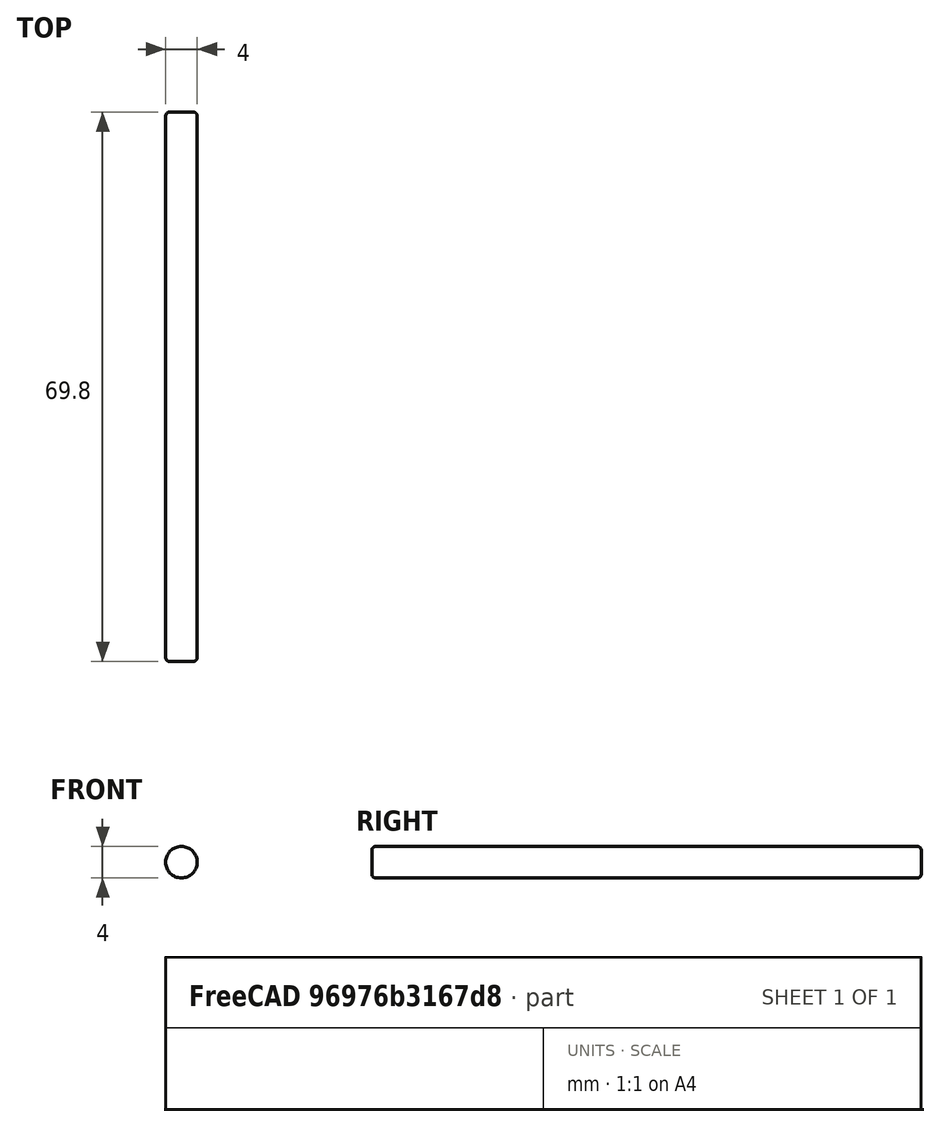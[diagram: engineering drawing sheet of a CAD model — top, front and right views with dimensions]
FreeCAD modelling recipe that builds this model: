
FCSTD DOCUMENT  (FreeCAD 0.19R24267 +99 (Git))
Label: Achse
License: All rights reserved
LicenseURL: http://en.wikipedia.org/wiki/All_rights_reserved
objects: TechDraw::DrawViewDimension×4, TechDraw::DrawProjGroupItem×3, Sketcher::SketchObject×1, PartDesign::Pad×1, PartDesign::Fillet×1, PartDesign::Body×1, TechDraw::DrawSVGTemplate×1, TechDraw::DrawProjGroup×1, TechDraw::DrawPage×1
note: 6 computed .brp shape members not serialized (recipe doc carries the construction recipe); baked Part::Feature solids carry a one-line shape summary decoded from their .brp

FEATURE [Sketcher::SketchObject] Sketch
  FullyConstrained = true
  MapMode = 5
  Placement = pos=(0,0,0) rot=(1,0,0;1.5708rad)
  Support = -> [XZ_Plane]
  sketch-geometry (1):
    g0: Circle CenterX=0 CenterY=0 CenterZ=0 NormalX=0 NormalY=0 NormalZ=1 AngleXU=0 Radius=2
  constraints (2):
    c: Coincident(g0,g-1)
    c: Diameter(g0) = 4
FEATURE [PartDesign::Pad] Pad
  Direction = (1,1,1)
  Length = 69.8
  Length2 = 100
  Placement = pos=(0,0,0) rot=(1,0,0;1.5708rad)
  Profile = -> Sketch
  Type = 0
FEATURE [PartDesign::Fillet] Fillet
  Base = -> Pad [Edge3,Edge2]
  BaseFeature = -> Pad
  Placement = pos=(0,0,0) rot=(1,0,0;1.5708rad)
  Radius = 0.5
  SupportTransform = false
FEATURE [PartDesign::Body] Body
  Group = -> [Sketch,Pad,Fillet]
  Origin = -> Origin
  Tip = -> Fillet
FEATURE [TechDraw::DrawSVGTemplate] Template
  EditableTexts = APPROVER_NAME=APPROVER NAME; AUTHOR_NAME=AUTHOR NAME; DATE=YYYY-MM-DD; DN=DN; DOCUMENT_TYPE=Mechanical assembly drawing; OWNER_NAME=OWNER NAME; PM=PM; PN=PN; REVISION=REV A; RIGHTS=(R) DO NOT DUPLICATE THIS DRAWING TO THIRD PARTIES WITHOUT OWNER'S PERMISSION !; SCALE=1:1; SHEET=99 of 99; SIZE=A4; TITLELINE-1=FreeCAD; TOLERANCE=+/- ?
  Height = 210
  Orientation = 1
  Width = 297
FEATURE [TechDraw::DrawProjGroupItem] ProjItem  label="Front"
  CoarseView = false
  Direction = (1,0,0)
  Focus = 100
  HardHidden = false
  IsoCount = 0
  IsoHidden = false
  IsoVisible = false
  LockPosition = true
  Perspective = false
  Rotation = 0
  RotationVector = (0,1,0)
  ScaleType = 2
  SeamHidden = false
  SeamVisible = true
  SmoothHidden = false
  SmoothVisible = true
  Source = -> [Body]
  Type = 0
  X = 0
  XDirection = (0,1,0)
  Y = 0
FEATURE [TechDraw::DrawProjGroupItem] ProjItem001  label="Left"
  CoarseView = false
  Direction = (1e-16,-1,0)
  Focus = 100
  HardHidden = false
  IsoCount = 0
  IsoHidden = false
  IsoVisible = false
  LockPosition = false
  Perspective = false
  Rotation = 0
  RotationVector = (1,0,0)
  ScaleType = 2
  SeamHidden = false
  SeamVisible = true
  SmoothHidden = false
  SmoothVisible = true
  Source = -> [Body]
  Type = 1
  X = 54.1874
  XDirection = (1,1e-16,0)
  Y = 0
FEATURE [TechDraw::DrawProjGroupItem] ProjItem002  label="Bottom"
  CoarseView = false
  Direction = (0,0,-1)
  Focus = 100
  HardHidden = false
  IsoCount = 0
  IsoHidden = false
  IsoVisible = false
  LockPosition = false
  Perspective = false
  Rotation = 0
  RotationVector = (1,0,0)
  ScaleType = 2
  SeamHidden = false
  SeamVisible = true
  SmoothHidden = false
  SmoothVisible = true
  Source = -> [Body]
  Type = 5
  X = 0
  XDirection = (0,1,0)
  Y = 36.1233
FEATURE [TechDraw::DrawProjGroup] ProjGroup
  Anchor = -> ProjItem
  AutoDistribute = true
  LockPosition = false
  ProjectionType = 0
  Rotation = 0
  ScaleType = 0
  Source = -> [Body]
  Views = -> [ProjItem,ProjItem001,ProjItem002]
  X = 148.5
  Y = 105
  spacingX = 15
  spacingY = 15
FEATURE [TechDraw::DrawViewDimension] Dimension
  Arbitrary = false
  ArbitraryTolerances = false
  EqualTolerance = true
  FormatSpec = %.2f
  FormatSpecOverTolerance = %+.2f
  FormatSpecUnderTolerance = %+.2f
  Inverted = false
  LockPosition = false
  MeasureType = 1
  OverTolerance = 0
  References2D = -> [ProjItem]
  Rotation = 0
  ScaleType = 0
  TheoreticalExact = false
  Type = 2
  UnderTolerance = 0
  X = 73.2859
  Y = -10.0646
FEATURE [TechDraw::DrawViewDimension] Dimension001
  Arbitrary = false
  ArbitraryTolerances = false
  EqualTolerance = true
  FormatSpec = %.2f
  FormatSpecOverTolerance = %+.2f
  FormatSpecUnderTolerance = %+.2f
  Inverted = false
  LockPosition = false
  MeasureType = 1
  OverTolerance = 0
  References2D = -> [ProjItem]
  Rotation = 0
  ScaleType = 0
  TheoreticalExact = false
  Type = 1
  UnderTolerance = 0
  X = -0.914962
  Y = -17.5118
FEATURE [TechDraw::DrawViewDimension] Dimension002
  Arbitrary = false
  ArbitraryTolerances = false
  EqualTolerance = true
  FormatSpec = %.2f
  FormatSpecOverTolerance = %+.2f
  FormatSpecUnderTolerance = %+.2f
  Inverted = false
  LockPosition = false
  MeasureType = 1
  OverTolerance = 0
  References2D = -> [ProjItem]
  Rotation = 0
  ScaleType = 0
  TheoreticalExact = false
  Type = 2
  UnderTolerance = 0
  X = -56.1516
  Y = -3.73977
FEATURE [TechDraw::DrawViewDimension] Dimension003
  Arbitrary = false
  ArbitraryTolerances = false
  EqualTolerance = true
  FormatSpec = %.2f
  FormatSpecOverTolerance = %+.2f
  FormatSpecUnderTolerance = %+.2f
  Inverted = false
  LockPosition = false
  MeasureType = 1
  OverTolerance = 0
  References2D = -> [ProjItem]
  Rotation = 0
  ScaleType = 0
  TheoreticalExact = false
  Type = 1
  UnderTolerance = 0
  X = -44.7146
  Y = 18.4481
FEATURE [TechDraw::DrawPage] Page
  KeepUpdated = true
  NextBalloonIndex = 1
  ProjectionType = 0
  Template = -> Template
  Views = -> [ProjGroup,Dimension,Dimension001,Dimension002,Dimension003]
